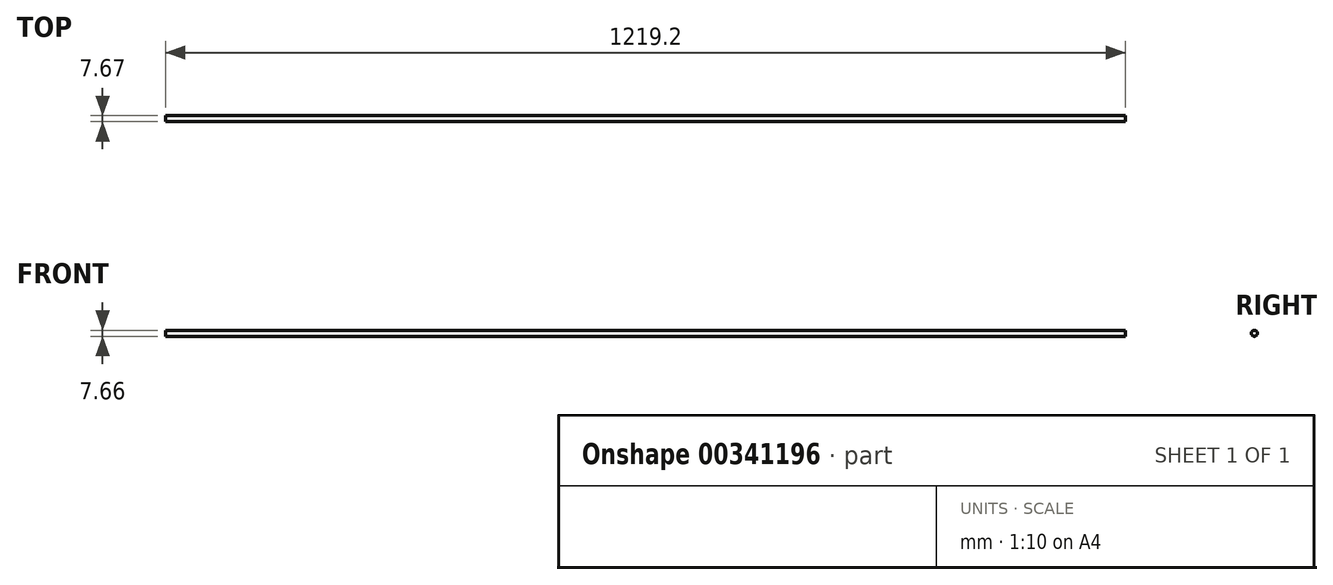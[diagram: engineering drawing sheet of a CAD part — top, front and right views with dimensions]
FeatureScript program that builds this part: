
annotation { "Feature Type Name" : "Feature", "Feature Type Description" : "" }
export const myFeature = defineFeature(function(context is Context, id is Id, definition is map)
    precondition{}
    {
        {
            var Q0;
            Q0=qCreatedBy(makeId("Right.planeOp"),FACE);
            var sketch = newSketch(context, id + "F0", { "sketchPlane" : qUnion([Q0])});
            skCircle(sketch, "E0", {"center": v(45.73, 0) * mm, "radius": 3.83 * mm});
            skSolve(sketch);
        }
        {
            var Q0;
            Q0=qSketchRegion(id+"F0",true);
            extrude(context, id + "F1", {"entities" : qUnion([Q0]), "endBound" : BoundingType.SYMMETRIC, "depth" : 1219.2 * mm});
        }
    });
